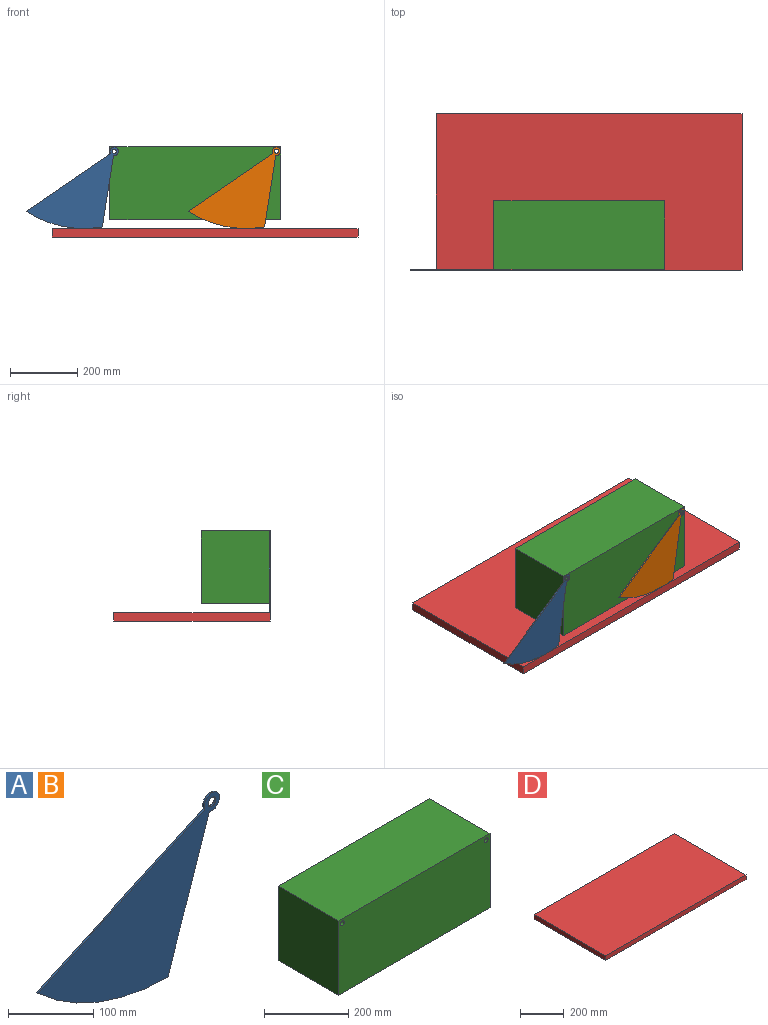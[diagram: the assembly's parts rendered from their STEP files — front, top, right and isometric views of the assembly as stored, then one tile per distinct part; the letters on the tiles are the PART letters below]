
ASSEMBLY  parts=4 mates=4
PART A: 7 faces, bbox 301.8x2.5x228.6 mm
  f0: cylinder r=317.5mm len=215.9mm, axis (0,1,0), area 603mm2, adj f1,f2,f3,f4
  f1: plane 203.87x69.15mm, normal (0.95,0,-0.32), area 546.8mm2, adj f0,f3,f4,f5
  f2: plane 277.56x125.95mm, normal (-0.41,0,0.91), area 774.2mm2, adj f0,f3,f4,f5
  f3: plane 301.83x228.6mm, normal (0,-1,0), area 30137.3mm2, adj f0,f1,f2,f5,f6
  f4: plane 301.83x228.6mm, normal (0,1,0), area 30137.3mm2, adj f0,f1,f2,f5,f6
  f5: cylinder r=12.7mm len=25.4mm, axis (0,-1,0), area 176.3mm2, adj f1,f2,f3,f4
  f6: cylinder r=6.35mm len=12.7mm, axis (0,-1,0), area 101.3mm2, adj f3,f4
PART B: same geometry as A
PART C: 8 faces, bbox 508x203.2x215.9 mm
  f0: plane 215.9x203.2mm, normal (-1,0,0), area 43870.9mm2, adj f1,f3,f4,f5
  f1: plane 508x203.2mm, normal (0,0,-1), area 103225.6mm2, adj f0,f2,f4,f5
  f2: plane 215.9x203.2mm, normal (1,0,0), area 43870.9mm2, adj f1,f3,f4,f5
  f3: plane 508x203.2mm, normal (0,0,1), area 103225.6mm2, adj f0,f2,f4,f5
  f4: plane 508x215.9mm, normal (0,-1,0), area 109423.8mm2, adj f0,f1,f2,f3,f6,f7
  f5: plane 508x215.9mm, normal (0,1,0), area 109423.8mm2, adj f0,f1,f2,f3,f6,f7
  f6: cylinder r=6.35mm len=203.2mm, axis (0,-1,0), area 8107.3mm2, adj f4,f5
  f7: cylinder r=6.35mm len=203.2mm, axis (0,-1,0), area 8107.3mm2, adj f4,f5
PART D: 6 faces, bbox 908.8x465.4x25.4 mm
  f0: plane 908.76x25.4mm, normal (0,1,0), area 23082.4mm2, adj f1,f3,f4,f5
  f1: plane 465.44x25.4mm, normal (-1,0,0), area 11822.2mm2, adj f0,f2,f4,f5
  f2: plane 908.76x25.4mm, normal (0,-1,0), area 23082.4mm2, adj f1,f3,f4,f5
  f3: plane 465.44x25.4mm, normal (1,0,0), area 11822.2mm2, adj f0,f2,f4,f5
  f4: plane 908.76x465.44mm, normal (0,0,-1), area 422972mm2, adj f0,f1,f2,f3
  f5: plane 908.76x465.44mm, normal (0,0,1), area 422972mm2, adj f0,f1,f2,f3
PLACE A rot(axis=(0,-1,0),9.9deg) t=(-245.97,-224.26,229.97)mm
PLACE B rot(axis=(0,-1,0),9.9deg) t=(236.63,-224.26,229.97)mm
PLACE C t=(-258.67,-121.39,26.77)mm
PLACE D at identity fixed
MATE parallel C.f1 <-> D.f5  axis (0,0,-1) through (-4.67,-121.39,26.77)mm
MATE parallel A.f2 <-> B.f2  axis (-0.56,0,0.83) through (-382.38,-224.26,136.97)mm
MATE revolute A.f6 <-> C.f7  axis (0,1,0) through (-245.97,-222.99,229.97)mm
MATE revolute B.f6 <-> C.f6  axis (0,1,0) through (236.63,-222.99,229.97)mm
